# Revit family: Desks-Teknion-LWBDP_Byward_Desk_with_Pedestal-R2019
name_source: partatom
category: Furniture
units: mm (PartAtom-declared; Revit-internal decimal feet)

## family parameters
Always vertical = Yes
Cut with Voids When Loaded = No
OmniClass Number = 23.40.20.00
OmniClass Title = General Furniture and Specialties
Room Calculation Point = No
Shared = Yes
Work Plane-Based = No

## types (3) — shared parameters
Assembly Code = E2020200
Manufacturer = Teknion
Manufacturer Fax = 416.661.4586
Metal Tab = 6.783 "
Part Number = LWBDP
Product Documentation Link = https://assets.teknion.com
Product Line = Byward
Product Page URL = https://www.teknion.com
Series = Byward
Sustainability Data = https://www.teknion.com
URL = www.teknion.com
Unit Weight URL = http://www.teknion.com
Warranty = http://www.teknion.com

## per-type parameters (varying)
| type | Depth | Description | Gable Cutout | Model | Storage Back |
| 24" Depth | 24 " | Byward Desk with Pedestal, 24" Depth | 3.19 " | LWBDP24___ | 2.06 " |
| 30" Depth | 30 " | Byward Desk with Pedestal, 30" Depth | 2.44 " | LWBDP30___ | 4.06 " |
| 36" Depth | 36 " | Byward Desk with Pedestal, 36" Depth | 1.44 " | LWBDP36___ | 4.06 " |

## geometry (parser evidence)
native form markers: Sweep x2
no freeform markers — native parametric forms only
